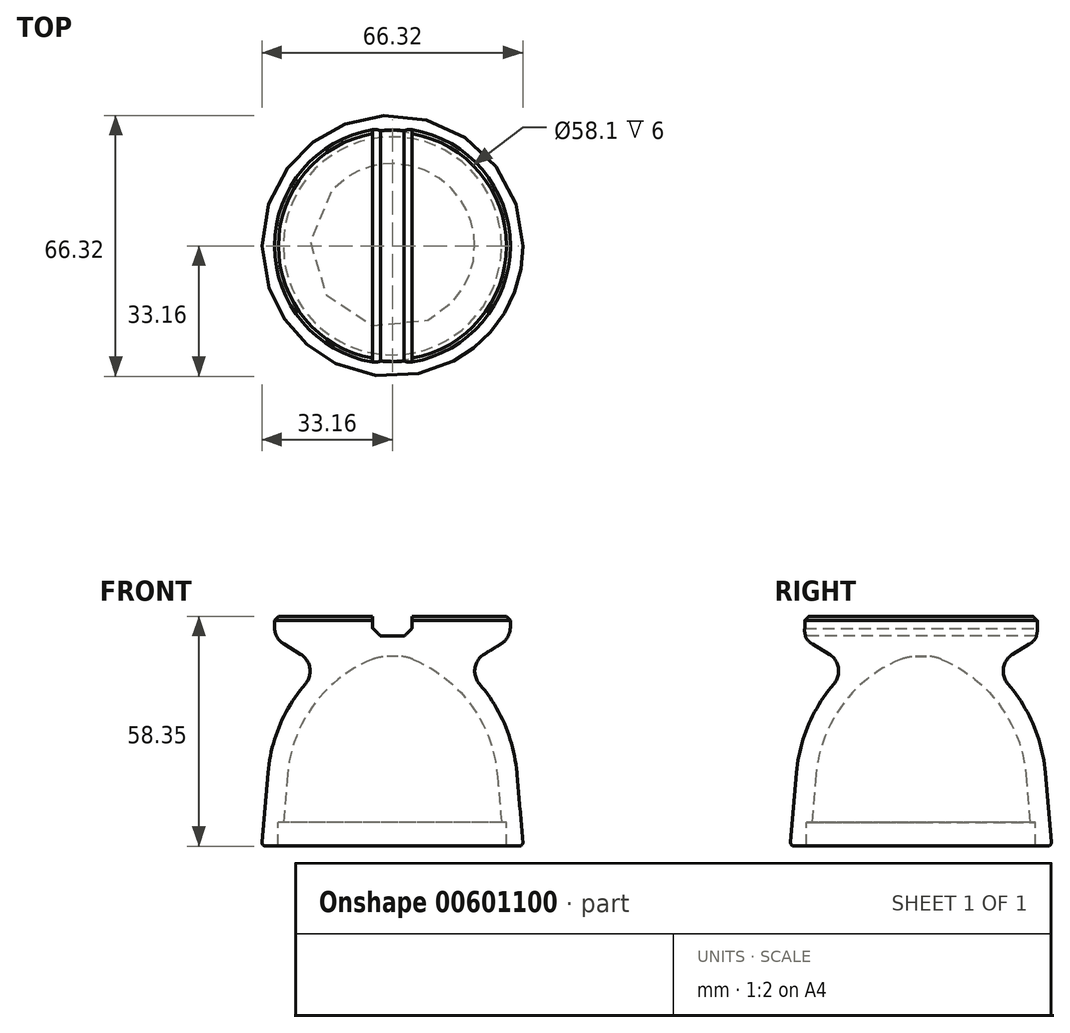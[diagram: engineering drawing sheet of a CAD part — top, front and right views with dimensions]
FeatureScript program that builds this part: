
annotation { "Feature Type Name" : "Feature", "Feature Type Description" : "" }
export const myFeature = defineFeature(function(context is Context, id is Id, definition is map)
    precondition{}
    {
        {
            var Q0;
            Q0=qCreatedBy(makeId("Front.planeOp"),FACE);
            var sketch = newSketch(context, id + "F0", { "sketchPlane" : qUnion([Q0])});
            skLineSegment(sketch, "E0", {"start": v(26.64, 20.02) * mm, "end": v(27.7, 7.82) * mm});
            skArc(sketch, "E1", {"start": v(26.64, 20.02) * mm, "mid": v(20.02, 37.64) * mm, "end": v(5.22, 49.28) * mm});
            skLineSegment(sketch, "E2", {"start": v(29.95, 57.43) * mm, "end": v(29.95, 59.17) * mm});
            skLineSegment(sketch, "E3", {"start": v(28.95, 60.17) * mm, "end": v(0, 60.17) * mm});
            skLineSegment(sketch, "E4.0", {"start": v(31.62, 20.46) * mm, "end": v(33.15, 2.9) * mm});
            skArc(sketch, "E4.1", {"start": v(31.62, 20.46) * mm, "mid": v(28.64, 32.5) * mm, "end": v(22.11, 43.04) * mm});
            skPoint(sketch, "E5.visualSharp", {"position": v(12.5, 45.17) * mm});
            skLineSegment(sketch, "E6", {"start": v(29.05, 1.82) * mm, "end": v(29.05, 7.82) * mm});
            skPoint(sketch, "E7.orphan", {"position": v(33.25, 1.82) * mm});
            skPoint(sketch, "E8.visualSharp", {"position": v(15.85, 48.91) * mm});
            skArc(sketch, "E8.filletArc", {"start": v(23.3, 50.56) * mm, "mid": v(20.97, 47.07) * mm, "end": v(22.11, 43.04) * mm});
            skLineSegment(sketch, "E9", {"start": v(23.3, 50.56) * mm, "end": v(27.56, 53.16) * mm});
            skPoint(sketch, "E10.visualSharp", {"position": v(29.95, 54.63) * mm});
            skArc(sketch, "E10.filletArc", {"start": v(27.56, 53.16) * mm, "mid": v(29.31, 54.98) * mm, "end": v(29.95, 57.43) * mm});
            skLineSegment(sketch, "E11", {"start": v(28.95, 60.17) * mm, "end": v(29.95, 59.17) * mm});
            skLineSegment(sketch, "E12", {"start": v(32.16, 1.82) * mm, "end": v(29.05, 1.82) * mm});
            skLineSegment(sketch, "E13", {"start": v(29.05, 7.82) * mm, "end": v(27.7, 7.82) * mm});
            skArc(sketch, "E14.filletArc", {"start": v(32.16, 1.82) * mm, "mid": v(32.9, 2.15) * mm, "end": v(33.15, 2.9) * mm});
            skLineSegment(sketch, "E15", {"start": v(0, 60.17) * mm, "end": v(0, 50.05) * mm});
            skLineSegment(sketch, "E16", {"start": v(1.38, 50.05) * mm, "end": v(0, 50.05) * mm});
            skPoint(sketch, "E17.visualSharp", {"position": v(3.2, 50.05) * mm});
            skArc(sketch, "E17.filletArc", {"start": v(5.22, 49.28) * mm, "mid": v(3.34, 49.86) * mm, "end": v(1.38, 50.05) * mm});
            skSolve(sketch);
        }
        {
            var Q0;
            Q0=makeQuery(id+"F0.imprint","IMPRINT",FACE,{"disambiguationData":[TD([[makeQuery(id+"F0.imprint","IMPRINT",EDGE,{"derivedFrom":sQuery(id+"F0.wireOp",EDGE,"E0")}),1.0]])]});
            var Q1;
            Q1=sQuery(id+"F0.wireOp",EDGE,"E15");
            revolve(context, id + "F1", {"entities" : qUnion([Q0]), "axis" : qUnion([Q1]), "revolveType" : RevolveType.FULL});
        }
        {
            var Q0;
            Q0=qCreatedBy(makeId("Front.planeOp"),FACE);
            var sketch = newSketch(context, id + "F2", { "sketchPlane" : qUnion([Q0])});
            skLineSegment(sketch, "E18.bottom", {"start": v(-5, 65.86) * mm, "end": v(5, 65.86) * mm});
            skLineSegment(sketch, "E18.top", {"start": v(-5, 55.17) * mm, "end": v(5, 55.17) * mm});
            skLineSegment(sketch, "E18.left", {"start": v(-5, 65.86) * mm, "end": v(-5, 55.17) * mm});
            skLineSegment(sketch, "E18.right", {"start": v(5, 65.86) * mm, "end": v(5, 55.17) * mm});
            skPoint(sketch, "E18.middle", {"position": v(0, 59.69) * mm});
            skSolve(sketch);
        }
        {
            var Q0;
            Q0=makeQuery(id+"F2.imprint","IMPRINT",FACE,{"disambiguationData":[TD([[makeQuery(id+"F2.imprint","IMPRINT",EDGE,{"derivedFrom":sQuery(id+"F2.wireOp",EDGE,"E18.bottom")}),-1.0]])]});
            extrude(context, id + "F3", {"entities" : qUnion([Q0]), "operationType" : NewBodyOperationType.REMOVE, "endBound" : BoundingType.SYMMETRIC, "oppositeDirection" : true, "depth" : 100 * mm, "offsetDistance" : 25 * mm});
        }
        {
            var Q0;
            Q0=makeQuery(id+"F3.boolean.opBoolean","COPY",EDGE,{"derivedFrom":makeQuery(id+"F3.opExtrude","SWEPT_EDGE",EDGE,{"disambiguationData":[OSD([sQuery(id+"F2.wireOp",EDGE,"E18.top"),sQuery(id+"F2.wireOp",EDGE,"E18.left")])]})});
            var Q1;
            Q1=makeQuery(id+"F3.boolean.opBoolean","COPY",EDGE,{"derivedFrom":makeQuery(id+"F3.opExtrude","SWEPT_EDGE",EDGE,{"disambiguationData":[OSD([sQuery(id+"F2.wireOp",EDGE,"E18.top"),sQuery(id+"F2.wireOp",EDGE,"E18.right")])]})});
            chamfer(context, id + "F4", {"entities" : qUnion([Q0, Q1]), "width" : 2 * mm, "tangentPropagation" : true});
        }
    });
